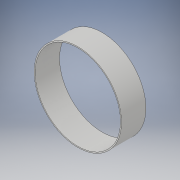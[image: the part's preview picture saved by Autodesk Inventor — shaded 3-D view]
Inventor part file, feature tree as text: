
AUTODESK INVENTOR PART (.ipt)
format: ipt  version: 2019 (Build 230136000, 136)  size: 104,960 bytes
history: native  units: mm
features: extrude x2, sketch x2
ambient origin geometry x8: Origin, YZ Plane, XZ Plane, XY Plane, X Axis, Y Axis, Z Axis, Center Point
bodies: Solid1 (feature_tree)
feature tree (4):
  extrude  "Extrusion1"  Depth=116.5mm TaperAngle=0.0deg
  extrude  "Extrusion2"  Depth=11.65mm TaperAngle=0.0deg
  sketch  "Sketch1"  dims[d0=418.0mm d1=116.5mm d2=0.0mm]
  sketch  "Sketch2"  dims[d3=408.0mm d4=11.65mm d5=0.0mm]
